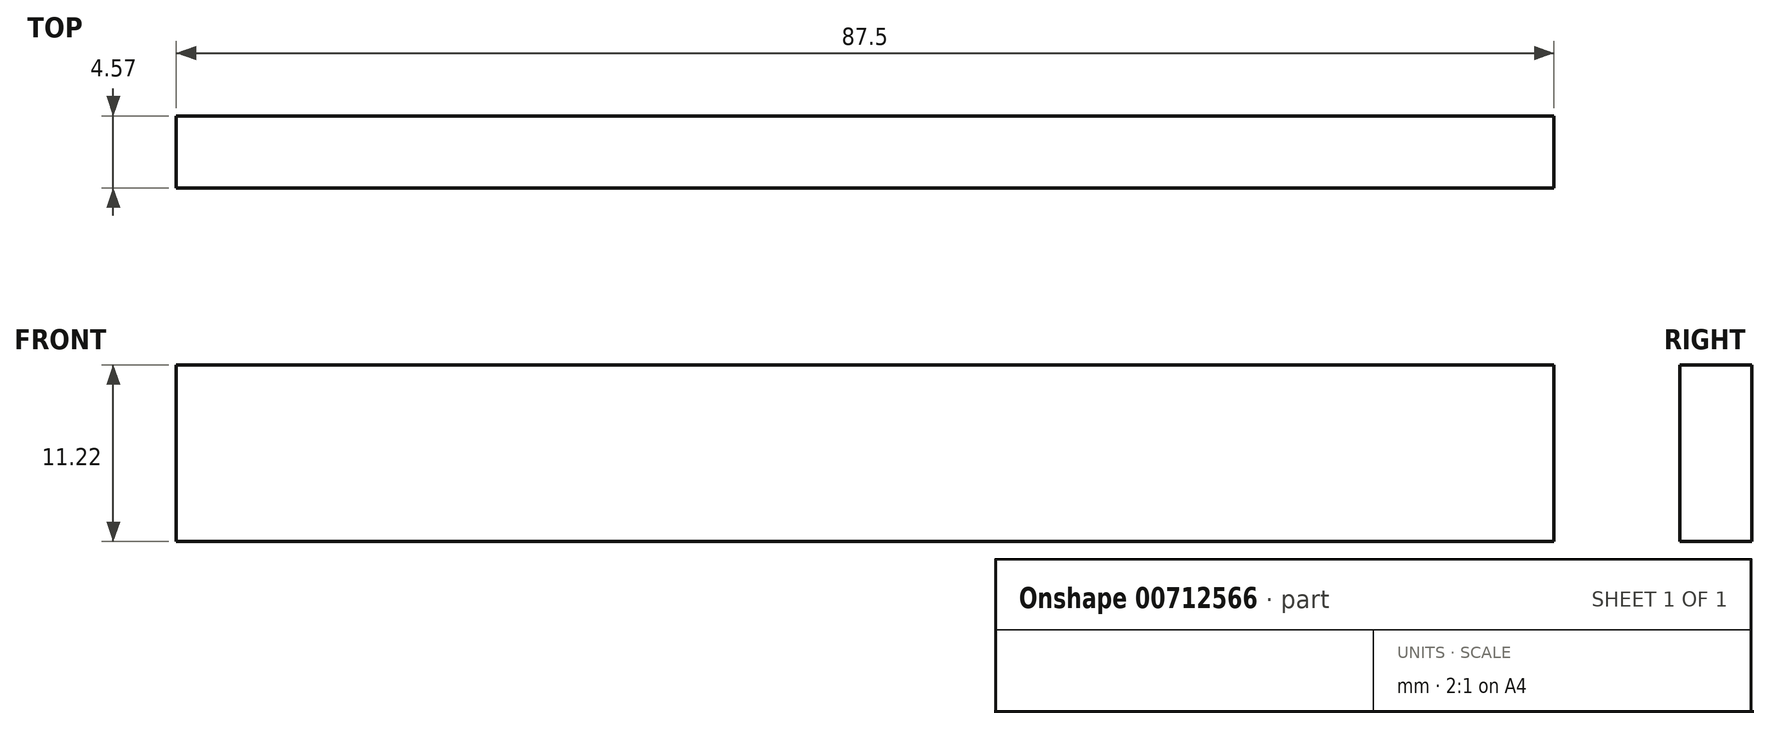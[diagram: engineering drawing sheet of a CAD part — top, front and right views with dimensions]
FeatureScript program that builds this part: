
annotation { "Feature Type Name" : "Feature", "Feature Type Description" : "" }
export const myFeature = defineFeature(function(context is Context, id is Id, definition is map)
    precondition{}
    {
        {
            var Q0;
            Q0=qCreatedBy(makeId("Front.planeOp"),FACE);
            var sketch = newSketch(context, id + "F0", { "sketchPlane" : qUnion([Q0])});
            skLineSegment(sketch, "E0.bottom", {"start": v(-48.2, 21.15) * mm, "end": v(39.29, 21.15) * mm});
            skLineSegment(sketch, "E0.top", {"start": v(-48.2, 9.93) * mm, "end": v(39.29, 9.93) * mm});
            skLineSegment(sketch, "E0.left", {"start": v(-48.2, 21.15) * mm, "end": v(-48.2, 9.93) * mm});
            skLineSegment(sketch, "E0.right", {"start": v(39.29, 21.15) * mm, "end": v(39.29, 9.93) * mm});
            skSolve(sketch);
        }
        {
            var Q0;
            Q0 = qSketchRegion(id + "F0", true);
            extrude(context, id + "F1", {"entities" : qUnion([Q0]), "oppositeDirection" : true, "depth" : 4.57 * mm, "offsetDistance" : 25.4 * mm});
        }
    });
